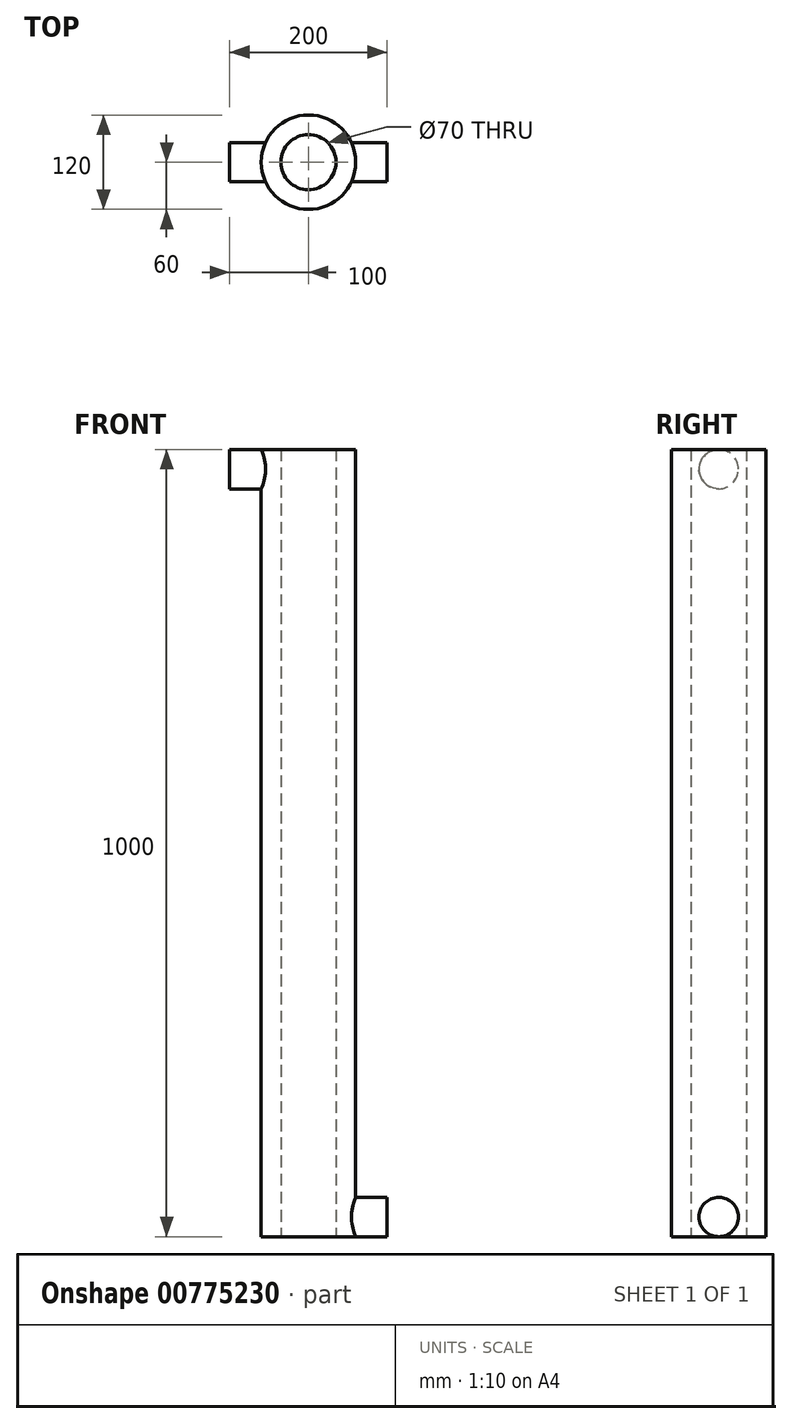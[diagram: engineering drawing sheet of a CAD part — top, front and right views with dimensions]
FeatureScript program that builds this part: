
annotation { "Feature Type Name" : "Feature", "Feature Type Description" : "" }
export const myFeature = defineFeature(function(context is Context, id is Id, definition is map)
    precondition{}
    {
        {
            var Q0;
            Q0=qCreatedBy(makeId("Top.planeOp"),FACE);
            var sketch = newSketch(context, id + "F0", { "sketchPlane" : qUnion([Q0])});
            skCircle(sketch, "E0", {"center": v(0, 0) * mm, "radius": 60 * mm});
            skCircle(sketch, "E1", {"center": v(0, 0) * mm, "radius": 25 * mm});
            skCircle(sketch, "E2", {"center": v(0, 0) * mm, "radius": 35 * mm});
            skSolve(sketch);
        }
        {
            var Q0;
            Q0=makeQuery(id+"F0.imprint","IMPRINT",FACE,{"disambiguationData":[TD([[makeQuery(id+"F0.imprint","IMPRINT",EDGE,{"derivedFrom":sQuery(id+"F0.wireOp",EDGE,"E0")}),1.0]])]});
            extrude(context, id + "F1", {"entities" : qUnion([Q0]), "endBound" : BoundingType.SYMMETRIC, "depth" : 1000 * mm, "offsetDistance" : 25 * mm});
        }
        {
            var Q0;
            Q0=qCreatedBy(makeId("Right.planeOp"),FACE);
            var sketch = newSketch(context, id + "F2", { "sketchPlane" : qUnion([Q0])});
            skCircle(sketch, "E3", {"center": v(0, 475) * mm, "radius": 25 * mm});
            skSolve(sketch);
        }
        {
            var Q0;
            Q0=qSketchRegion(id+"F2",true);
            var Q1;
            Q1=makeQuery(id+"F1.opExtrude","SWEPT_FACE",FACE,{"disambiguationData":[OSD([sQuery(id+"F0.wireOp",EDGE,"E0")])]});
            extrude(context, id + "F3", {"entities" : qUnion([Q0]), "operationType" : NewBodyOperationType.ADD, "oppositeDirection" : true, "depth" : 100 * mm, "offsetDistance" : 25 * mm, "hasSecondDirection" : true, "secondDirectionBound" : SecondDirectionBoundingType.UP_TO_SURFACE, "secondDirectionOppositeDirection" : true, "secondDirectionDepth" : 25 * mm, "secondDirectionBoundEntityFace" : qUnion([Q1]), "hasSecondDirectionOffset" : true, "secondDirectionOffsetDistance" : 0 * mm});
        }
        {
            var Q0;
            Q0=qCreatedBy(makeId("Right.planeOp"),FACE);
            var sketch = newSketch(context, id + "F4", { "sketchPlane" : qUnion([Q0])});
            skCircle(sketch, "E4", {"center": v(0, -475) * mm, "radius": 25 * mm});
            skSolve(sketch);
        }
        {
            var Q0;
            Q0 = qSketchRegion(id + "F4", true);
            var Q1;
            Q1=makeQuery(id+"F1.opExtrude","SWEPT_FACE",FACE,{"disambiguationData":[OSD([sQuery(id+"F0.wireOp",EDGE,"E0")])]});
            extrude(context, id + "F5", {"entities" : qUnion([Q0]), "operationType" : NewBodyOperationType.ADD, "depth" : 100 * mm, "offsetDistance" : 25 * mm, "hasSecondDirection" : true, "secondDirectionBound" : SecondDirectionBoundingType.UP_TO_SURFACE, "secondDirectionOppositeDirection" : false, "secondDirectionDepth" : 0 * mm, "secondDirectionBoundEntityFace" : qUnion([Q1]), "hasSecondDirectionOffset" : true, "secondDirectionOffsetDistance" : 0 * mm});
        }
    });
